# Revit family: J315
name_source: partatom
category: Lighting Fixtures
revit_build: Autodesk Revit Architecture 2012 (Build: 20110309_2315(x64)
units: mm (PartAtom-declared; Revit-internal decimal feet)

## types (3) — shared parameters
Aperture = 3 1/2"
Color Filter = 16777215
Cone Finish = J315 Cone : Gold cone
Default Elevation = 48"
Depth = 6 3/4"
Description = Lens Wall Wash, 3 1/2 inch Square Aperture
Dimming Lamp Color Temperature Shift = <None>
Emit from Line Length = 1"
Finish = Matte Black
Lamp = LED Lamp
Length = 16 1/16"
Manufacturer = Kurtversen Lighting
Manufacturer Fax = (201)-664-4801
Model = J315
Product Documentation Link = http://www.kurtversen.com
Product Page URL = http://www.kurtversen.com
Tilt Angle = -90.00°
URL = http://www.kurtversen.com
Voltage = 120 V
Width = 16 1/4"
ceiling thickness = -1 1/2"

## per-type parameters (varying)
| type | Apparent Load | Photometric Web File | Wattage Comments |
| J315_13W_Xicato_1100_lm_3000K | 13 VA | J315_13W_Xicato_1100_lm_3000K.ies | 13W |
| J315_18W_Xicato_1500_lm_3000K | 18 VA | J315_18W_Xicato_1500_lm_3000K.ies | 18W |
| J315_24W_Xicato_2100_lm_3000K | 24 VA | J315_24W_Xicato_2100_lm_3000K.ies | 24W |

## geometry (parser evidence)
native form markers: Blend x10, Sweep x4
no freeform markers — native parametric forms only
